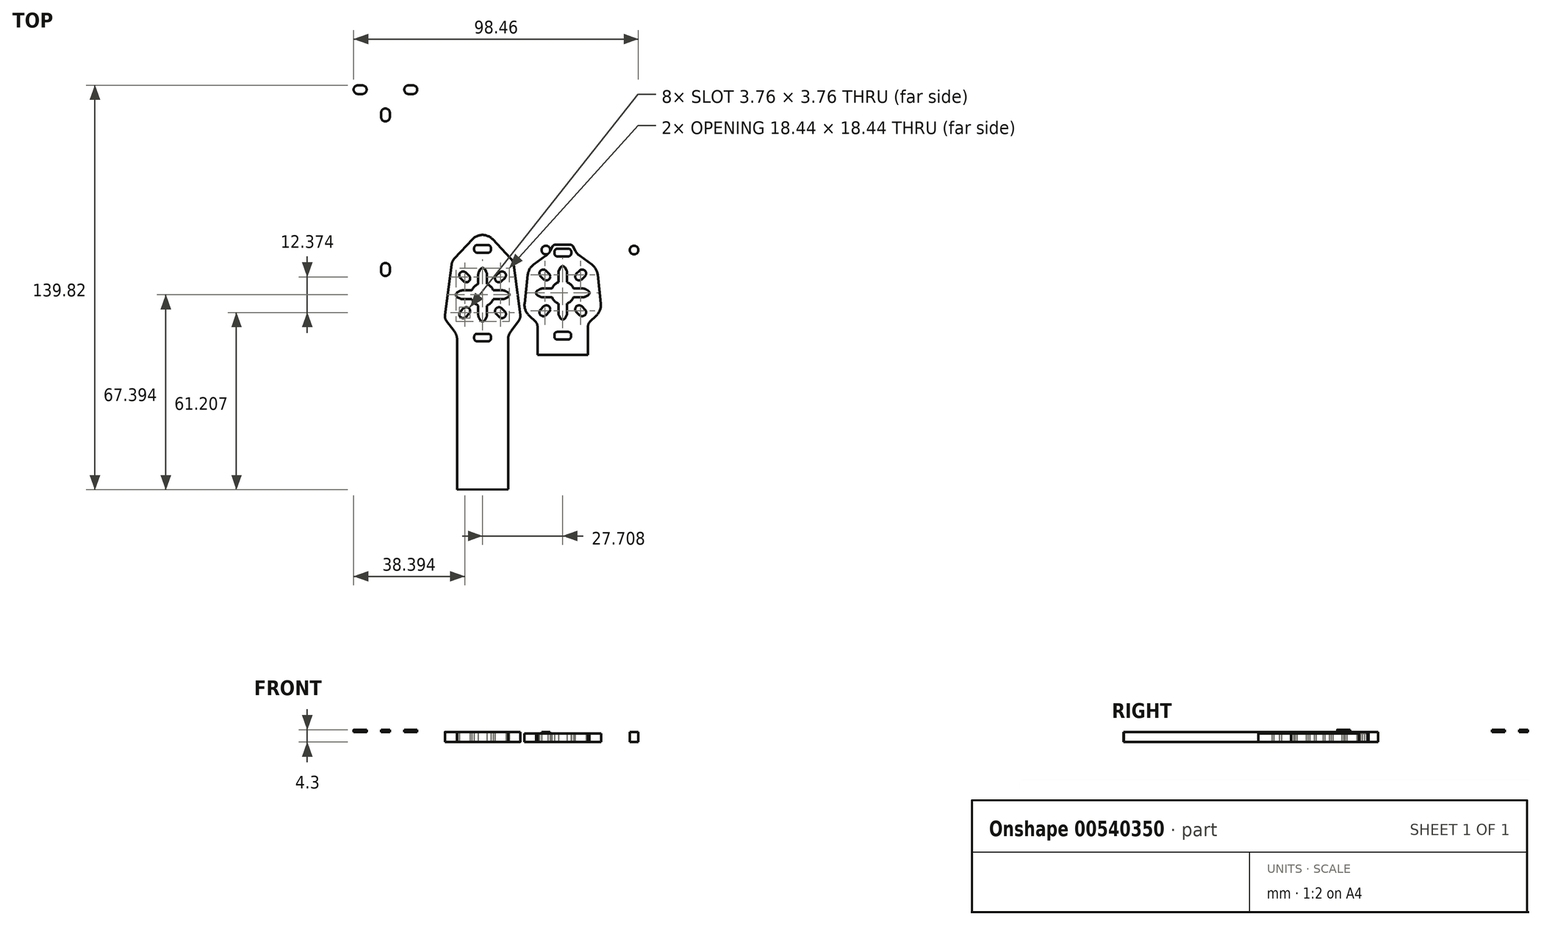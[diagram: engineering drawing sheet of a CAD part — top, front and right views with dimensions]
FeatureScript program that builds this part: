
annotation { "Feature Type Name" : "Feature", "Feature Type Description" : "" }
export const myFeature = defineFeature(function(context is Context, id is Id, definition is map)
    precondition{}
    {
        {
            var Q0;
            Q0=qCreatedBy(makeId("Top.planeOp"),FACE);
            var sketch = newSketch(context, id + "F0", { "sketchPlane" : qUnion([Q0])});
            skCircle(sketch, "E0", {"center": v(0, 0) * mm, "radius": 100 * mm, "construction": true});
            skLineSegment(sketch, "E1.bottom", {"start": v(16, -18) * mm, "end": v(-16, -18) * mm, "construction": true});
            skLineSegment(sketch, "E1.top", {"start": v(16, 18) * mm, "end": v(-16, 18) * mm, "construction": true});
            skLineSegment(sketch, "E1.left", {"start": v(18, -16) * mm, "end": v(18, 16) * mm, "construction": true});
            skLineSegment(sketch, "E1.right", {"start": v(-18, -16) * mm, "end": v(-18, 16) * mm, "construction": true});
            skLineSegment(sketch, "E2", {"start": v(0, 0) * mm, "end": v(-63.94, 63.94) * mm, "construction": true});
            skCircle(sketch, "E3", {"center": v(-15.25, 15.25) * mm, "radius": 1.5 * mm});
            skPoint(sketch, "E4", {"position": v(-37.13, -0.22) * mm});
            skPoint(sketch, "E5.visualSharp", {"position": v(-37.13, -74.76) * mm});
            skArc(sketch, "E5.filletArc", {"start": v(-16, 18) * mm, "mid": v(-17.41, 17.41) * mm, "end": v(-18, 16) * mm, "construction": true});
            skPoint(sketch, "E6.visualSharp", {"position": v(18, 18) * mm});
            skArc(sketch, "E6.filletArc", {"start": v(18, 16) * mm, "mid": v(17.41, 17.41) * mm, "end": v(16, 18) * mm, "construction": true});
            skPoint(sketch, "E7.visualSharp", {"position": v(18, -18) * mm});
            skArc(sketch, "E7.filletArc", {"start": v(16, -18) * mm, "mid": v(17.41, -17.41) * mm, "end": v(18, -16) * mm, "construction": true});
            skPoint(sketch, "E8.visualSharp", {"position": v(-18, -18) * mm});
            skArc(sketch, "E8.filletArc", {"start": v(-18, -16) * mm, "mid": v(-17.41, -17.41) * mm, "end": v(-16, -18) * mm, "construction": true});
            skCircle(sketch, "E9.MirrorC", {"center": v(15.25, 15.25) * mm, "radius": 1.5 * mm});
            skLineSegment(sketch, "E10.bottom", {"start": v(10, -10) * mm, "end": v(-10, -10) * mm, "construction": true});
            skLineSegment(sketch, "E10.top", {"start": v(10, 10) * mm, "end": v(-10, 10) * mm, "construction": true});
            skLineSegment(sketch, "E10.left", {"start": v(10, -10) * mm, "end": v(10, 10) * mm, "construction": true});
            skLineSegment(sketch, "E10.right", {"start": v(-10, -10) * mm, "end": v(-10, 10) * mm, "construction": true});
            skCircle(sketch, "E11", {"center": v(-37.13, -0.22) * mm, "radius": 13.85 * mm, "construction": true});
            skLineSegment(sketch, "E12", {"start": v(-37.13, -0.22) * mm, "end": v(-25.82, -11.53) * mm, "construction": true});
            skArc(sketch, "E13", {"start": v(-30.52, -4.92) * mm, "mid": v(-32.43, -4.92) * mm, "end": v(-32.43, -6.83) * mm});
            skArc(sketch, "E14", {"start": v(-31.37, -7.89) * mm, "mid": v(-29.46, -7.89) * mm, "end": v(-29.46, -5.98) * mm});
            skLineSegment(sketch, "E15", {"start": v(-37.13, -0.22) * mm, "end": v(-58.36, -21.45) * mm, "construction": true});
            skLineSegment(sketch, "E16", {"start": v(-32.43, -6.83) * mm, "end": v(-31.37, -7.89) * mm});
            skLineSegment(sketch, "E17.MirrorCS", {"start": v(-30.52, -4.92) * mm, "end": v(-29.46, -5.98) * mm});
            skLineSegment(sketch, "E18.MirrorCS", {"start": v(-43.74, -4.92) * mm, "end": v(-44.8, -5.98) * mm});
            skArc(sketch, "E19.MirrorCS", {"start": v(-42.9, -7.89) * mm, "mid": v(-44.8, -7.89) * mm, "end": v(-44.8, -5.98) * mm});
            skLineSegment(sketch, "E20.MirrorCS", {"start": v(-41.83, -6.83) * mm, "end": v(-42.9, -7.89) * mm});
            skArc(sketch, "E21.MirrorCS", {"start": v(-43.74, -4.92) * mm, "mid": v(-41.83, -4.92) * mm, "end": v(-41.83, -6.83) * mm});
            skLineSegment(sketch, "E22.MirrorCS", {"start": v(-41.83, 6.4) * mm, "end": v(-42.9, 7.46) * mm});
            skLineSegment(sketch, "E23.MirrorCS", {"start": v(-43.74, 4.49) * mm, "end": v(-44.8, 5.55) * mm});
            skArc(sketch, "E24.MirrorCS", {"start": v(-43.74, 4.49) * mm, "mid": v(-41.83, 4.49) * mm, "end": v(-41.83, 6.4) * mm});
            skArc(sketch, "E25.MirrorCS", {"start": v(-42.9, 7.46) * mm, "mid": v(-44.8, 7.46) * mm, "end": v(-44.8, 5.55) * mm});
            skLineSegment(sketch, "E26.MirrorCS", {"start": v(-32.43, 6.4) * mm, "end": v(-31.37, 7.46) * mm});
            skLineSegment(sketch, "E27.MirrorCS", {"start": v(-30.52, 4.49) * mm, "end": v(-29.46, 5.55) * mm});
            skArc(sketch, "E28.MirrorCS", {"start": v(-31.37, 7.46) * mm, "mid": v(-29.46, 7.46) * mm, "end": v(-29.46, 5.55) * mm});
            skArc(sketch, "E29.MirrorCS", {"start": v(-30.52, 4.49) * mm, "mid": v(-32.43, 4.49) * mm, "end": v(-32.43, 6.4) * mm});
            skLineSegment(sketch, "E30", {"start": v(-26.4, 10.18) * mm, "end": v(-24.12, -7.13) * mm});
            skPoint(sketch, "E31.visualSharp", {"position": v(-26.77, 13.06) * mm});
            skPoint(sketch, "E32.MirrorP", {"position": v(-51, -9.33) * mm});
            skLineSegment(sketch, "E33", {"start": v(-34.22, 15.95) * mm, "end": v(-34.22, 15.34) * mm});
            skLineSegment(sketch, "E34", {"start": v(-40.03, 15.95) * mm, "end": v(-40.03, 15.34) * mm});
            skArc(sketch, "E35", {"start": v(-35.63, -3.92) * mm, "mid": v(-34.3, -3.04) * mm, "end": v(-33.42, -1.72) * mm});
            skLineSegment(sketch, "E36.bottom", {"start": v(-44.11, 1.28) * mm, "end": v(-40.84, 1.28) * mm});
            skLineSegment(sketch, "E36.top", {"start": v(-44.11, -1.72) * mm, "end": v(-40.84, -1.72) * mm});
            skLineSegment(sketch, "E37.left", {"start": v(-38.63, 6.77) * mm, "end": v(-38.63, 3.5) * mm});
            skLineSegment(sketch, "E37.right", {"start": v(-35.63, 6.77) * mm, "end": v(-35.63, 3.5) * mm});
            skLineSegment(sketch, "E38.trimOffspring", {"start": v(-33.42, -1.72) * mm, "end": v(-30.15, -1.72) * mm});
            skLineSegment(sketch, "E39.trimOffspring", {"start": v(-33.42, 1.28) * mm, "end": v(-30.15, 1.28) * mm});
            skLineSegment(sketch, "E40.trimOffspring", {"start": v(-35.63, -3.92) * mm, "end": v(-35.63, -7.2) * mm});
            skLineSegment(sketch, "E41.trimOffspring", {"start": v(-38.63, -3.92) * mm, "end": v(-38.63, -7.2) * mm});
            skArc(sketch, "E42.trimOffspring", {"start": v(-33.42, 1.28) * mm, "mid": v(-34.3, 2.61) * mm, "end": v(-35.63, 3.5) * mm});
            skArc(sketch, "E43.trimOffspring", {"start": v(-38.63, 3.5) * mm, "mid": v(-39.96, 2.61) * mm, "end": v(-40.84, 1.28) * mm});
            skArc(sketch, "E44.trimOffspring", {"start": v(-40.84, -1.72) * mm, "mid": v(-39.96, -3.04) * mm, "end": v(-38.63, -3.92) * mm});
            skArc(sketch, "E45", {"start": v(-27.85, -0.73) * mm, "mid": v(-27.8, -0.7) * mm, "end": v(-27.75, -0.66) * mm});
            skPoint(sketch, "E46.visualSharp", {"position": v(-29.63, -1.72) * mm});
            skArc(sketch, "E46.filletArc", {"start": v(-30.15, -1.72) * mm, "mid": v(-29.65, -1.65) * mm, "end": v(-29.18, -1.46) * mm});
            skPoint(sketch, "E47.visualSharp", {"position": v(-29.63, 1.28) * mm});
            skArc(sketch, "E47.filletArc", {"start": v(-29.18, 1.03) * mm, "mid": v(-29.65, 1.22) * mm, "end": v(-30.15, 1.28) * mm});
            skArc(sketch, "E48.MirrorCS", {"start": v(-45.08, 1.03) * mm, "mid": v(-44.61, 1.22) * mm, "end": v(-44.11, 1.28) * mm});
            skArc(sketch, "E49.MirrorCS", {"start": v(-44.11, -1.72) * mm, "mid": v(-44.61, -1.65) * mm, "end": v(-45.08, -1.46) * mm});
            skArc(sketch, "E50.MirrorCS", {"start": v(-46.4, -0.73) * mm, "mid": v(-46.46, -0.7) * mm, "end": v(-46.5, -0.66) * mm});
            skPoint(sketch, "E51.MirrorP", {"position": v(-44.63, 1.28) * mm});
            skArc(sketch, "E52.MirrorCS", {"start": v(-35.88, -8.17) * mm, "mid": v(-35.7, -7.7) * mm, "end": v(-35.63, -7.2) * mm});
            skArc(sketch, "E53.MirrorCS", {"start": v(-38.63, -7.2) * mm, "mid": v(-38.56, -7.7) * mm, "end": v(-38.38, -8.17) * mm});
            skPoint(sketch, "E54.MirrorP", {"position": v(-35.63, -7.72) * mm});
            skPoint(sketch, "E55.MirrorP", {"position": v(-38.63, -7.72) * mm});
            skArc(sketch, "E56.MirrorCS", {"start": v(-38.63, 6.77) * mm, "mid": v(-38.56, 7.27) * mm, "end": v(-38.38, 7.74) * mm});
            skArc(sketch, "E57.MirrorCS", {"start": v(-35.88, 7.74) * mm, "mid": v(-35.7, 7.27) * mm, "end": v(-35.63, 6.77) * mm});
            skPoint(sketch, "E58.MirrorP", {"position": v(-35.63, 7.28) * mm});
            skPoint(sketch, "E59.MirrorP", {"position": v(-38.63, 7.28) * mm});
            skPoint(sketch, "E60.visualSharp", {"position": v(-34.22, 16.34) * mm});
            skPoint(sketch, "E61.visualSharp", {"position": v(-34.22, 14.34) * mm});
            skArc(sketch, "E61.filletArc", {"start": v(-35.22, 14.34) * mm, "mid": v(-34.52, 14.63) * mm, "end": v(-34.22, 15.34) * mm});
            skPoint(sketch, "E62.visualSharp", {"position": v(-40.03, 14.34) * mm});
            skArc(sketch, "E62.filletArc", {"start": v(-40.03, 15.34) * mm, "mid": v(-39.74, 14.63) * mm, "end": v(-39.03, 14.34) * mm});
            skPoint(sketch, "E63.orphan", {"position": v(-44.63, -1.72) * mm});
            skCircle(sketch, "E64", {"center": v(-37.13, -0.22) * mm, "radius": 8 * mm, "construction": true});
            skLineSegment(sketch, "E65", {"start": v(-27.45, 12.4) * mm, "end": v(-33.62, 18.95) * mm});
            skPoint(sketch, "E66.visualSharp", {"position": v(-26.56, 11.46) * mm});
            skArc(sketch, "E66.filletArc", {"start": v(-26.4, 10.18) * mm, "mid": v(-26.74, 11.37) * mm, "end": v(-27.45, 12.4) * mm});
            skLineSegment(sketch, "E67", {"start": v(-37.13, -0.22) * mm, "end": v(-37.13, -33.93) * mm, "construction": true});
            skLineSegment(sketch, "E68.MirrorCS", {"start": v(-46.8, 12.4) * mm, "end": v(-40.63, 18.95) * mm});
            skLineSegment(sketch, "E69", {"start": v(-24.7, -9.34) * mm, "end": v(-27.3, -12.78) * mm});
            skPoint(sketch, "E70.visualSharp", {"position": v(-23.96, -8.36) * mm});
            skArc(sketch, "E70.filletArc", {"start": v(-24.7, -9.34) * mm, "mid": v(-24.2, -8.3) * mm, "end": v(-24.12, -7.13) * mm});
            skPoint(sketch, "E71.visualSharp", {"position": v(-30.8, -17.37) * mm});
            skArc(sketch, "E72", {"start": v(-33.62, 18.95) * mm, "mid": v(-37.13, 20.46) * mm, "end": v(-40.63, 18.95) * mm});
            skPoint(sketch, "E73.MirrorP", {"position": v(-50.3, -8.36) * mm});
            skPoint(sketch, "E74.MirrorCS.start.orphan", {"position": v(-28.33, -14.12) * mm});
            skPoint(sketch, "E75.MirrorCS.end.orphan", {"position": v(-44.01, -18.06) * mm});
            skPoint(sketch, "E75.MirrorCS.start.orphan", {"position": v(-45.93, -14.12) * mm});
            skPoint(sketch, "E76.MirrorCS.end.orphan", {"position": v(-44.01, -21.74) * mm});
            skPoint(sketch, "E77.end.orphan", {"position": v(-30.25, -21.74) * mm});
            skPoint(sketch, "E77.start.orphan", {"position": v(-30.25, -18.06) * mm});
            skLineSegment(sketch, "E78", {"start": v(-28.33, -15.8) * mm, "end": v(-28.33, -21.65) * mm});
            skArc(sketch, "E79.filletArc", {"start": v(-27.3, -12.78) * mm, "mid": v(-28.06, -14.2) * mm, "end": v(-28.33, -15.8) * mm});
            skPoint(sketch, "E80.visualSharp", {"position": v(-49.56, -9.34) * mm});
            skPoint(sketch, "E81.MirrorCS.start.orphan", {"position": v(-47.87, 10.18) * mm});
            skPoint(sketch, "E82.MirrorCS.end.orphan", {"position": v(-46.8, 12.4) * mm});
            skLineSegment(sketch, "E83.MirrorCS", {"start": v(-47.87, 10.18) * mm, "end": v(-50.14, -7.13) * mm});
            skArc(sketch, "E84.MirrorCS", {"start": v(-47.87, 10.18) * mm, "mid": v(-47.51, 11.37) * mm, "end": v(-46.8, 12.4) * mm});
            skArc(sketch, "E85.MirrorCS", {"start": v(-49.56, -9.34) * mm, "mid": v(-50.07, -8.3) * mm, "end": v(-50.14, -7.13) * mm});
            skLineSegment(sketch, "E86.MirrorCS", {"start": v(-49.56, -9.34) * mm, "end": v(-46.95, -12.78) * mm});
            skArc(sketch, "E87.MirrorCS", {"start": v(-46.95, -12.78) * mm, "mid": v(-46.2, -14.2) * mm, "end": v(-45.93, -15.8) * mm});
            skLineSegment(sketch, "E88.MirrorCS", {"start": v(-45.93, -15.8) * mm, "end": v(-45.93, -21.65) * mm});
            skLineSegment(sketch, "E89", {"start": v(-39.03, 14.34) * mm, "end": v(-35.22, 14.34) * mm});
            skLineSegment(sketch, "E90", {"start": v(-37.13, 15.64) * mm, "end": v(-39.72, 15.64) * mm, "construction": true});
            skArc(sketch, "E91.MirrorCS", {"start": v(-35.22, 16.95) * mm, "mid": v(-34.52, 16.65) * mm, "end": v(-34.22, 15.95) * mm});
            skArc(sketch, "E92.MirrorCS", {"start": v(-40.03, 15.95) * mm, "mid": v(-39.74, 16.65) * mm, "end": v(-39.03, 16.95) * mm});
            skLineSegment(sketch, "E93.MirrorCS", {"start": v(-39.03, 16.95) * mm, "end": v(-35.22, 16.95) * mm});
            skLineSegment(sketch, "E94", {"start": v(-70.71, 70.71) * mm, "end": v(-89.86, 51.56) * mm, "construction": true});
            skLineSegment(sketch, "E95.MirrorCS", {"start": v(-39.03, -13.7) * mm, "end": v(-35.22, -13.7) * mm});
            skArc(sketch, "E96.MirrorCS", {"start": v(-40.03, -14.7) * mm, "mid": v(-39.74, -14) * mm, "end": v(-39.03, -13.7) * mm});
            skArc(sketch, "E97.MirrorCS", {"start": v(-35.22, -13.7) * mm, "mid": v(-34.52, -14) * mm, "end": v(-34.22, -14.7) * mm});
            skLineSegment(sketch, "E98.MirrorCS", {"start": v(-39.03, -16.32) * mm, "end": v(-35.22, -16.32) * mm});
            skArc(sketch, "E99.MirrorCS", {"start": v(-40.03, -15.32) * mm, "mid": v(-39.74, -16.03) * mm, "end": v(-39.03, -16.32) * mm});
            skArc(sketch, "E100.MirrorCS", {"start": v(-35.22, -16.32) * mm, "mid": v(-34.52, -16.03) * mm, "end": v(-34.22, -15.32) * mm});
            skLineSegment(sketch, "E101.MirrorCS", {"start": v(-34.22, -15.32) * mm, "end": v(-34.22, -14.7) * mm});
            skLineSegment(sketch, "E102.MirrorCS", {"start": v(-40.03, -15.32) * mm, "end": v(-40.03, -14.7) * mm});
            skLineSegment(sketch, "E103", {"start": v(-28.33, -21.65) * mm, "end": v(-28.33, -67.5) * mm});
            skLineSegment(sketch, "E104", {"start": v(-45.93, -21.65) * mm, "end": v(-45.93, -67.6) * mm});
            skLineSegment(sketch, "E105", {"start": v(-45.93, -67.6) * mm, "end": v(-28.33, -67.5) * mm});
            skLineSegment(sketch, "E106", {"start": v(-38.38, 7.74) * mm, "end": v(-37.94, 8.52) * mm});
            skLineSegment(sketch, "E107.trimOffspring", {"start": v(-37.13, -9.2) * mm, "end": v(-37.13, 20.66) * mm, "construction": true});
            skPoint(sketch, "E108.trimOffspring.end.orphan", {"position": v(-46.4, 0.3) * mm});
            skLineSegment(sketch, "E109.MirrorCS", {"start": v(-38.38, -8.17) * mm, "end": v(-37.94, -8.96) * mm});
            skPoint(sketch, "E110.orphan", {"position": v(-36.61, -9.5) * mm});
            skPoint(sketch, "E111.MirrorCS.start.orphan", {"position": v(-37.64, -9.5) * mm});
            skLineSegment(sketch, "E112.MirrorCS", {"start": v(-35.88, 7.74) * mm, "end": v(-36.32, 8.52) * mm});
            skArc(sketch, "E113", {"start": v(-36.32, 8.52) * mm, "mid": v(-37.13, 9) * mm, "end": v(-37.94, 8.52) * mm});
            skLineSegment(sketch, "E114.MirrorCS", {"start": v(-35.88, -8.17) * mm, "end": v(-36.32, -8.96) * mm});
            skArc(sketch, "E115.MirrorCS", {"start": v(-36.32, -8.96) * mm, "mid": v(-37.13, -9.43) * mm, "end": v(-37.94, -8.96) * mm});
            skLineSegment(sketch, "E116.MirrorCS", {"start": v(-29.18, 1.03) * mm, "end": v(-28.39, 0.6) * mm});
            skLineSegment(sketch, "E117.MirrorCS", {"start": v(-29.18, -1.46) * mm, "end": v(-28.39, -1.03) * mm});
            skArc(sketch, "E118.MirrorCS", {"start": v(-28.39, 0.6) * mm, "mid": v(-27.91, -0.22) * mm, "end": v(-28.39, -1.03) * mm});
            skLineSegment(sketch, "E119.MirrorCS", {"start": v(-45.08, 1.03) * mm, "end": v(-45.87, 0.6) * mm});
            skLineSegment(sketch, "E120.MirrorCS", {"start": v(-45.08, -1.46) * mm, "end": v(-45.87, -1.03) * mm});
            skArc(sketch, "E121.MirrorCS", {"start": v(-45.87, 0.6) * mm, "mid": v(-46.35, -0.22) * mm, "end": v(-45.87, -1.03) * mm});
            skSolve(sketch);
        }
        {
            var Q0;
            Q0 = qSketchRegion(id + "F0", true);
            extrude(context, id + "F1", {"entities" : qUnion([Q0]), "depth" : 3.5 * mm, "offsetDistance" : 25.4 * mm});
        }
        {
            var Q0;
            Q0=makeQuery(id+"F1.opExtrude","CAP_FACE",FACE,{"disambiguationData":[OSD([sQuery(id+"F0.wireOp",EDGE,"E13"),sQuery(id+"F0.wireOp",EDGE,"E14"),sQuery(id+"F0.wireOp",EDGE,"E16"),sQuery(id+"F0.wireOp",EDGE,"E17.MirrorCS"),sQuery(id+"F0.wireOp",EDGE,"E18.MirrorCS"),sQuery(id+"F0.wireOp",EDGE,"E19.MirrorCS"),sQuery(id+"F0.wireOp",EDGE,"E20.MirrorCS"),sQuery(id+"F0.wireOp",EDGE,"E21.MirrorCS"),sQuery(id+"F0.wireOp",EDGE,"E22.MirrorCS"),sQuery(id+"F0.wireOp",EDGE,"E23.MirrorCS"),sQuery(id+"F0.wireOp",EDGE,"E24.MirrorCS"),sQuery(id+"F0.wireOp",EDGE,"E25.MirrorCS"),sQuery(id+"F0.wireOp",EDGE,"E26.MirrorCS"),sQuery(id+"F0.wireOp",EDGE,"E27.MirrorCS"),sQuery(id+"F0.wireOp",EDGE,"E28.MirrorCS"),sQuery(id+"F0.wireOp",EDGE,"E29.MirrorCS"),sQuery(id+"F0.wireOp",EDGE,"E30"),sQuery(id+"F0.wireOp",EDGE,"E33"),sQuery(id+"F0.wireOp",EDGE,"E34"),sQuery(id+"F0.wireOp",EDGE,"E35"),sQuery(id+"F0.wireOp",EDGE,"E36.bottom"),sQuery(id+"F0.wireOp",EDGE,"E36.top"),sQuery(id+"F0.wireOp",EDGE,"E37.left"),sQuery(id+"F0.wireOp",EDGE,"E37.right"),sQuery(id+"F0.wireOp",EDGE,"E38.trimOffspring"),sQuery(id+"F0.wireOp",EDGE,"E39.trimOffspring"),sQuery(id+"F0.wireOp",EDGE,"E40.trimOffspring"),sQuery(id+"F0.wireOp",EDGE,"E41.trimOffspring"),sQuery(id+"F0.wireOp",EDGE,"E42.trimOffspring"),sQuery(id+"F0.wireOp",EDGE,"E43.trimOffspring"),sQuery(id+"F0.wireOp",EDGE,"E44.trimOffspring"),sQuery(id+"F0.wireOp",EDGE,"E46.filletArc"),sQuery(id+"F0.wireOp",EDGE,"E47.filletArc"),sQuery(id+"F0.wireOp",EDGE,"E48.MirrorCS"),sQuery(id+"F0.wireOp",EDGE,"E49.MirrorCS"),sQuery(id+"F0.wireOp",EDGE,"E52.MirrorCS"),sQuery(id+"F0.wireOp",EDGE,"E53.MirrorCS"),sQuery(id+"F0.wireOp",EDGE,"E56.MirrorCS"),sQuery(id+"F0.wireOp",EDGE,"E57.MirrorCS"),sQuery(id+"F0.wireOp",EDGE,"E61.filletArc"),sQuery(id+"F0.wireOp",EDGE,"E62.filletArc"),sQuery(id+"F0.wireOp",EDGE,"E65"),sQuery(id+"F0.wireOp",EDGE,"E66.filletArc"),sQuery(id+"F0.wireOp",EDGE,"E68.MirrorCS"),sQuery(id+"F0.wireOp",EDGE,"E69"),sQuery(id+"F0.wireOp",EDGE,"E70.filletArc"),sQuery(id+"F0.wireOp",EDGE,"E72"),sQuery(id+"F0.wireOp",EDGE,"E78"),sQuery(id+"F0.wireOp",EDGE,"E79.filletArc"),sQuery(id+"F0.wireOp",EDGE,"E83.MirrorCS"),sQuery(id+"F0.wireOp",EDGE,"E84.MirrorCS"),sQuery(id+"F0.wireOp",EDGE,"E85.MirrorCS"),sQuery(id+"F0.wireOp",EDGE,"E86.MirrorCS"),sQuery(id+"F0.wireOp",EDGE,"E87.MirrorCS"),sQuery(id+"F0.wireOp",EDGE,"E88.MirrorCS"),sQuery(id+"F0.wireOp",EDGE,"E89"),sQuery(id+"F0.wireOp",EDGE,"E91.MirrorCS"),sQuery(id+"F0.wireOp",EDGE,"E92.MirrorCS"),sQuery(id+"F0.wireOp",EDGE,"E93.MirrorCS"),sQuery(id+"F0.wireOp",EDGE,"E95.MirrorCS"),sQuery(id+"F0.wireOp",EDGE,"E96.MirrorCS"),sQuery(id+"F0.wireOp",EDGE,"E97.MirrorCS"),sQuery(id+"F0.wireOp",EDGE,"E98.MirrorCS"),sQuery(id+"F0.wireOp",EDGE,"E99.MirrorCS"),sQuery(id+"F0.wireOp",EDGE,"E100.MirrorCS"),sQuery(id+"F0.wireOp",EDGE,"E101.MirrorCS"),sQuery(id+"F0.wireOp",EDGE,"E102.MirrorCS"),sQuery(id+"F0.wireOp",EDGE,"E103"),sQuery(id+"F0.wireOp",EDGE,"E104"),sQuery(id+"F0.wireOp",EDGE,"E105"),sQuery(id+"F0.wireOp",EDGE,"E106"),sQuery(id+"F0.wireOp",EDGE,"E109.MirrorCS"),sQuery(id+"F0.wireOp",EDGE,"E112.MirrorCS"),sQuery(id+"F0.wireOp",EDGE,"E113"),sQuery(id+"F0.wireOp",EDGE,"E114.MirrorCS"),sQuery(id+"F0.wireOp",EDGE,"E115.MirrorCS"),sQuery(id+"F0.wireOp",EDGE,"E116.MirrorCS"),sQuery(id+"F0.wireOp",EDGE,"E117.MirrorCS"),sQuery(id+"F0.wireOp",EDGE,"E118.MirrorCS"),sQuery(id+"F0.wireOp",EDGE,"E119.MirrorCS"),sQuery(id+"F0.wireOp",EDGE,"E120.MirrorCS"),sQuery(id+"F0.wireOp",EDGE,"E121.MirrorCS")])],"isStart":false});
            var sketch = newSketch(context, id + "F2", { "sketchPlane" : qUnion([Q0])});
            skArc(sketch, "E122", {"start": v(-40.92, 1.05) * mm, "mid": v(-41.13, -0.22) * mm, "end": v(-40.92, -1.48) * mm});
            skArc(sketch, "E123.trimOffspring", {"start": v(-35.79, 3.55) * mm, "mid": v(-37.13, 3.78) * mm, "end": v(-38.47, 3.55) * mm});
            skArc(sketch, "E124.trimOffspring", {"start": v(-33.34, -1.48) * mm, "mid": v(-33.13, -0.22) * mm, "end": v(-33.34, 1.05) * mm});
            skArc(sketch, "E125.trimOffspring", {"start": v(-38.47, -3.98) * mm, "mid": v(-37.13, -4.22) * mm, "end": v(-35.79, -3.98) * mm});
            skArc(sketch, "E126", {"start": v(-69.21, 9.28) * mm, "mid": v(-70.71, 10.78) * mm, "end": v(-72.21, 9.28) * mm});
            skPoint(sketch, "E127.center.orphan", {"position": v(-70.71, 7.78) * mm});
            skArc(sketch, "E128", {"start": v(-72.21, 7.78) * mm, "mid": v(-70.71, 6.28) * mm, "end": v(-69.21, 7.78) * mm});
            skLineSegment(sketch, "E129", {"start": v(-69.21, 9.28) * mm, "end": v(-69.21, 7.78) * mm});
            skLineSegment(sketch, "E130", {"start": v(-72.21, 9.28) * mm, "end": v(-72.21, 7.78) * mm});
            skArc(sketch, "E131", {"start": v(-32.49, 10.63) * mm, "mid": v(-36.77, 11.58) * mm, "end": v(-41.1, 10.9) * mm});
            skLineSegment(sketch, "E132", {"start": v(-38.47, 3.55) * mm, "end": v(-41.3, 6.38) * mm});
            skLineSegment(sketch, "E133", {"start": v(-40.92, 1.05) * mm, "end": v(-43.75, 3.88) * mm});
            skArc(sketch, "E134", {"start": v(-41.3, 6.38) * mm, "mid": v(-43.79, 6.37) * mm, "end": v(-43.75, 3.88) * mm});
            skArc(sketch, "E135", {"start": v(-42.27, 8.55) * mm, "mid": v(-43.34, 7.83) * mm, "end": v(-44.32, 6.97) * mm});
            skLineSegment(sketch, "E136", {"start": v(-41.77, 9.95) * mm, "end": v(-41.77, 9.42) * mm});
            skPoint(sketch, "E137.visualSharp", {"position": v(-41.77, 8.83) * mm});
            skArc(sketch, "E137.filletArc", {"start": v(-42.27, 8.55) * mm, "mid": v(-41.9, 8.92) * mm, "end": v(-41.77, 9.42) * mm});
            skPoint(sketch, "E138.visualSharp", {"position": v(-41.77, 10.63) * mm});
            skArc(sketch, "E138.filletArc", {"start": v(-41.1, 10.9) * mm, "mid": v(-41.59, 10.53) * mm, "end": v(-41.77, 9.95) * mm});
            skLineSegment(sketch, "E139.MirrorCS", {"start": v(-66.07, 80.88) * mm, "end": v(-66.07, 80.34) * mm});
            skArc(sketch, "E140.MirrorCS", {"start": v(-65.57, 79.48) * mm, "mid": v(-65.94, 79.85) * mm, "end": v(-66.07, 80.34) * mm});
            skArc(sketch, "E141.MirrorCS", {"start": v(-65.57, 79.48) * mm, "mid": v(-64.5, 78.75) * mm, "end": v(-63.52, 77.9) * mm});
            skPoint(sketch, "E142.MirrorP", {"position": v(-66.07, 79.75) * mm});
            skPoint(sketch, "E143.MirrorP", {"position": v(-66.07, 81.56) * mm});
            skPoint(sketch, "E144.MirrorP", {"position": v(-32.49, 10.63) * mm});
            skArc(sketch, "E145.MirrorCS", {"start": v(-66.73, 81.82) * mm, "mid": v(-66.25, 81.45) * mm, "end": v(-66.07, 80.88) * mm});
            skLineSegment(sketch, "E146.MirrorCS", {"start": v(-69.37, 74.48) * mm, "end": v(-66.54, 77.3) * mm});
            skArc(sketch, "E147.MirrorCS", {"start": v(-66.54, 77.3) * mm, "mid": v(-64.05, 77.3) * mm, "end": v(-64.09, 74.8) * mm});
            skLineSegment(sketch, "E148.MirrorCS", {"start": v(-66.92, 71.98) * mm, "end": v(-64.09, 74.8) * mm});
            skLineSegment(sketch, "E149.MirrorCS", {"start": v(-66.07, 60.54) * mm, "end": v(-66.07, 61.08) * mm});
            skLineSegment(sketch, "E150.MirrorCS", {"start": v(-75.35, 60.54) * mm, "end": v(-75.35, 61.08) * mm});
            skArc(sketch, "E151.MirrorCS", {"start": v(-75.85, 61.94) * mm, "mid": v(-75.49, 61.57) * mm, "end": v(-75.35, 61.08) * mm});
            skPoint(sketch, "E152.MirrorP", {"position": v(-66.07, 59.86) * mm});
            skArc(sketch, "E153.MirrorCS", {"start": v(-74.7, 59.6) * mm, "mid": v(-75.17, 59.97) * mm, "end": v(-75.35, 60.54) * mm});
            skArc(sketch, "E154.MirrorCS", {"start": v(-66.73, 59.6) * mm, "mid": v(-66.25, 59.97) * mm, "end": v(-66.07, 60.54) * mm});
            skArc(sketch, "E155.MirrorCS", {"start": v(-65.57, 61.94) * mm, "mid": v(-65.94, 61.57) * mm, "end": v(-66.07, 61.08) * mm});
            skArc(sketch, "E156.MirrorCS", {"start": v(-74.88, 64.11) * mm, "mid": v(-77.37, 64.13) * mm, "end": v(-77.33, 66.61) * mm});
            skArc(sketch, "E157.MirrorCS", {"start": v(-75.85, 61.94) * mm, "mid": v(-76.92, 62.67) * mm, "end": v(-77.9, 63.52) * mm});
            skPoint(sketch, "E158.MirrorP", {"position": v(-75.35, 61.67) * mm});
            skLineSegment(sketch, "E159.MirrorCS", {"start": v(-69.21, 61.21) * mm, "end": v(-69.21, 62.71) * mm});
            skArc(sketch, "E160.MirrorCS", {"start": v(-69.37, 66.94) * mm, "mid": v(-70.71, 66.71) * mm, "end": v(-72.05, 66.94) * mm});
            skLineSegment(sketch, "E161.MirrorCS", {"start": v(-72.21, 61.21) * mm, "end": v(-72.21, 62.71) * mm});
            skArc(sketch, "E162.MirrorCS", {"start": v(-72.21, 62.71) * mm, "mid": v(-70.71, 64.21) * mm, "end": v(-69.21, 62.71) * mm});
            skPoint(sketch, "E163.MirrorP", {"position": v(-75.35, 59.86) * mm});
            skArc(sketch, "E164.MirrorCS", {"start": v(-65.57, 61.94) * mm, "mid": v(-64.5, 62.67) * mm, "end": v(-63.52, 63.52) * mm});
            skLineSegment(sketch, "E165.MirrorCS", {"start": v(-72.05, 66.94) * mm, "end": v(-74.88, 64.11) * mm});
            skPoint(sketch, "E166.MirrorP", {"position": v(-66.07, 61.67) * mm});
            skArc(sketch, "E167.MirrorCS", {"start": v(-69.21, 61.21) * mm, "mid": v(-70.71, 59.71) * mm, "end": v(-72.21, 61.21) * mm});
            skArc(sketch, "E168.MirrorCS", {"start": v(-66.54, 64.11) * mm, "mid": v(-64.05, 64.13) * mm, "end": v(-64.09, 66.61) * mm});
            skLineSegment(sketch, "E169.MirrorCS", {"start": v(-69.37, 66.94) * mm, "end": v(-66.54, 64.11) * mm});
            skLineSegment(sketch, "E170.MirrorCS", {"start": v(-74.5, 69.44) * mm, "end": v(-77.33, 66.61) * mm});
            skLineSegment(sketch, "E171.MirrorCS", {"start": v(-66.92, 69.44) * mm, "end": v(-64.09, 66.61) * mm});
            skArc(sketch, "E172.MirrorCS", {"start": v(-66.07, 59.86) * mm, "mid": v(-70.35, 58.92) * mm, "end": v(-74.7, 59.6) * mm});
            skLineSegment(sketch, "E173.MirrorCS", {"start": v(-60.54, 75.35) * mm, "end": v(-61.08, 75.35) * mm});
            skLineSegment(sketch, "E174.MirrorCS", {"start": v(-60.54, 66.07) * mm, "end": v(-61.08, 66.07) * mm});
            skArc(sketch, "E175.MirrorCS", {"start": v(-61.94, 75.85) * mm, "mid": v(-61.57, 75.49) * mm, "end": v(-61.08, 75.35) * mm});
            skArc(sketch, "E176.MirrorCS", {"start": v(-59.6, 66.73) * mm, "mid": v(-59.97, 66.25) * mm, "end": v(-60.54, 66.07) * mm});
            skArc(sketch, "E177.MirrorCS", {"start": v(-59.6, 74.7) * mm, "mid": v(-59.97, 75.17) * mm, "end": v(-60.54, 75.35) * mm});
            skPoint(sketch, "E178.MirrorP", {"position": v(-59.86, 75.35) * mm});
            skArc(sketch, "E179.MirrorCS", {"start": v(-61.94, 65.57) * mm, "mid": v(-61.57, 65.94) * mm, "end": v(-61.08, 66.07) * mm});
            skArc(sketch, "E180.MirrorCS", {"start": v(-61.94, 65.57) * mm, "mid": v(-62.67, 64.5) * mm, "end": v(-63.52, 63.52) * mm});
            skLineSegment(sketch, "E181.MirrorCS", {"start": v(-61.21, 72.21) * mm, "end": v(-62.71, 72.21) * mm});
            skPoint(sketch, "E182.MirrorP", {"position": v(-61.67, 66.07) * mm});
            skArc(sketch, "E183.MirrorCS", {"start": v(-59.6, 74.7) * mm, "mid": v(-58.91, 70.71) * mm, "end": v(-59.6, 66.73) * mm});
            skPoint(sketch, "E184.MirrorP", {"position": v(-59.86, 66.07) * mm});
            skPoint(sketch, "E185.MirrorP", {"position": v(-62.71, 70.71) * mm});
            skArc(sketch, "E186.MirrorCS", {"start": v(-61.94, 75.85) * mm, "mid": v(-62.67, 76.92) * mm, "end": v(-63.52, 77.9) * mm});
            skPoint(sketch, "E187.MirrorP", {"position": v(-61.67, 75.35) * mm});
            skLineSegment(sketch, "E188.MirrorCS", {"start": v(-61.21, 69.21) * mm, "end": v(-62.71, 69.21) * mm});
            skArc(sketch, "E189.MirrorCS", {"start": v(-61.21, 72.21) * mm, "mid": v(-59.71, 70.71) * mm, "end": v(-61.21, 69.21) * mm});
            skArc(sketch, "E190.MirrorCS", {"start": v(-62.71, 69.21) * mm, "mid": v(-64.21, 70.71) * mm, "end": v(-62.71, 72.21) * mm});
            skLineSegment(sketch, "E191.MirrorCS", {"start": v(-80.21, 72.21) * mm, "end": v(-78.71, 72.21) * mm});
            skLineSegment(sketch, "E192.MirrorCS", {"start": v(-80.21, 69.21) * mm, "end": v(-78.71, 69.21) * mm});
            skArc(sketch, "E193.MirrorCS", {"start": v(-78.71, 69.21) * mm, "mid": v(-77.21, 70.71) * mm, "end": v(-78.71, 72.21) * mm});
            skArc(sketch, "E194.MirrorCS", {"start": v(-80.21, 72.21) * mm, "mid": v(-81.71, 70.71) * mm, "end": v(-80.21, 69.21) * mm});
            skLineSegment(sketch, "E195.MirrorCS", {"start": v(-75.35, 80.88) * mm, "end": v(-75.35, 80.34) * mm});
            skArc(sketch, "E196.MirrorCS", {"start": v(-75.85, 79.48) * mm, "mid": v(-75.49, 79.85) * mm, "end": v(-75.35, 80.34) * mm});
            skArc(sketch, "E197.MirrorCS", {"start": v(-74.7, 81.82) * mm, "mid": v(-75.17, 81.45) * mm, "end": v(-75.35, 80.88) * mm});
            skPoint(sketch, "E198.MirrorP", {"position": v(-75.35, 81.56) * mm});
            skArc(sketch, "E199.MirrorCS", {"start": v(-75.85, 79.48) * mm, "mid": v(-76.92, 78.75) * mm, "end": v(-77.9, 77.9) * mm});
            skPoint(sketch, "E200.MirrorP", {"position": v(-75.35, 79.75) * mm});
            skArc(sketch, "E201.MirrorCS", {"start": v(-45.9, 4.92) * mm, "mid": v(-45.17, 6) * mm, "end": v(-44.32, 6.97) * mm});
            skLineSegment(sketch, "E202.MirrorCS", {"start": v(-80.88, 66.07) * mm, "end": v(-80.34, 66.07) * mm});
            skArc(sketch, "E203.MirrorCS", {"start": v(-79.48, 65.57) * mm, "mid": v(-79.85, 65.94) * mm, "end": v(-80.34, 66.07) * mm});
            skPoint(sketch, "E204.MirrorP", {"position": v(-79.75, 66.07) * mm});
            skPoint(sketch, "E205.MirrorP", {"position": v(-81.56, 66.07) * mm});
            skArc(sketch, "E206.MirrorCS", {"start": v(-79.48, 65.57) * mm, "mid": v(-78.75, 64.5) * mm, "end": v(-77.9, 63.52) * mm});
            skLineSegment(sketch, "E207.MirrorCS", {"start": v(-80.88, 75.35) * mm, "end": v(-80.34, 75.35) * mm});
            skArc(sketch, "E208.MirrorCS", {"start": v(-81.82, 74.7) * mm, "mid": v(-81.45, 75.17) * mm, "end": v(-80.88, 75.35) * mm});
            skArc(sketch, "E209.MirrorCS", {"start": v(-79.48, 75.85) * mm, "mid": v(-79.85, 75.49) * mm, "end": v(-80.34, 75.35) * mm});
            skPoint(sketch, "E210.MirrorP", {"position": v(-81.56, 75.35) * mm});
            skPoint(sketch, "E211.MirrorP", {"position": v(-79.75, 75.35) * mm});
            skArc(sketch, "E212.MirrorCS", {"start": v(-81.82, 74.7) * mm, "mid": v(-82.51, 70.71) * mm, "end": v(-81.82, 66.73) * mm});
            skArc(sketch, "E213.MirrorCS", {"start": v(-81.82, 66.73) * mm, "mid": v(-81.45, 66.25) * mm, "end": v(-80.88, 66.07) * mm});
            skSolve(sketch);
        }
        {
            var Q0;
            Q0 = qSketchRegion(id + "F2", true);
            extrude(context, id + "F3", {"entities" : qUnion([Q0]), "depth" : 0.8 * mm, "offsetDistance" : 25 * mm});
        }
        {
            var Q0;
            Q0=qCreatedBy(makeId("Top.planeOp"),FACE);
            var sketch = newSketch(context, id + "F4", { "sketchPlane" : qUnion([Q0])});
            skPoint(sketch, "E214.visualSharp", {"position": v(8.94, -5.4) * mm});
            skCircle(sketch, "E215", {"center": v(-9.42, 0.43) * mm, "radius": 13.85 * mm, "construction": true});
            skLineSegment(sketch, "E216", {"start": v(-9.42, 0.43) * mm, "end": v(1.9, -10.88) * mm, "construction": true});
            skArc(sketch, "E217", {"start": v(-2.8, -4.27) * mm, "mid": v(-4.72, -4.27) * mm, "end": v(-4.72, -6.18) * mm});
            skArc(sketch, "E218", {"start": v(-3.66, -7.24) * mm, "mid": v(-1.75, -7.24) * mm, "end": v(-1.75, -5.33) * mm});
            skLineSegment(sketch, "E219", {"start": v(-4.72, -6.18) * mm, "end": v(-3.66, -7.24) * mm});
            skLineSegment(sketch, "E220.MirrorCS", {"start": v(-2.8, -4.27) * mm, "end": v(-1.75, -5.33) * mm});
            skLineSegment(sketch, "E221.MirrorCS", {"start": v(-16.03, -4.27) * mm, "end": v(-17.1, -5.33) * mm});
            skArc(sketch, "E222.MirrorCS", {"start": v(-15.18, -7.24) * mm, "mid": v(-17.1, -7.24) * mm, "end": v(-17.1, -5.33) * mm});
            skLineSegment(sketch, "E223.MirrorCS", {"start": v(-14.12, -6.18) * mm, "end": v(-15.18, -7.24) * mm});
            skArc(sketch, "E224.MirrorCS", {"start": v(-16.03, -4.27) * mm, "mid": v(-14.12, -4.27) * mm, "end": v(-14.12, -6.18) * mm});
            skLineSegment(sketch, "E225.MirrorCS", {"start": v(-14.12, 7.05) * mm, "end": v(-15.18, 8.1) * mm});
            skLineSegment(sketch, "E226.MirrorCS", {"start": v(-16.03, 5.14) * mm, "end": v(-17.1, 6.2) * mm});
            skArc(sketch, "E227.MirrorCS", {"start": v(-16.03, 5.14) * mm, "mid": v(-14.12, 5.14) * mm, "end": v(-14.12, 7.05) * mm});
            skArc(sketch, "E228.MirrorCS", {"start": v(-15.18, 8.1) * mm, "mid": v(-17.1, 8.1) * mm, "end": v(-17.1, 6.2) * mm});
            skLineSegment(sketch, "E229.MirrorCS", {"start": v(-4.72, 7.05) * mm, "end": v(-3.66, 8.1) * mm});
            skLineSegment(sketch, "E230.MirrorCS", {"start": v(-2.8, 5.14) * mm, "end": v(-1.75, 6.2) * mm});
            skArc(sketch, "E231.MirrorCS", {"start": v(-3.66, 8.1) * mm, "mid": v(-1.75, 8.1) * mm, "end": v(-1.75, 6.2) * mm});
            skArc(sketch, "E232.MirrorCS", {"start": v(-2.8, 5.14) * mm, "mid": v(-4.72, 5.14) * mm, "end": v(-4.72, 7.05) * mm});
            skLineSegment(sketch, "E233", {"start": v(-6.48, 14.68) * mm, "end": v(-6.48, 14.07) * mm});
            skLineSegment(sketch, "E234", {"start": v(-12.3, 14.68) * mm, "end": v(-12.3, 14.07) * mm});
            skArc(sketch, "E235", {"start": v(-7.92, -3.27) * mm, "mid": v(-6.6, -2.4) * mm, "end": v(-5.71, -1.07) * mm});
            skLineSegment(sketch, "E236.bottom", {"start": v(-16.4, 1.93) * mm, "end": v(-13.13, 1.93) * mm});
            skLineSegment(sketch, "E236.top", {"start": v(-16.4, -1.07) * mm, "end": v(-13.13, -1.07) * mm});
            skLineSegment(sketch, "E237.left", {"start": v(-10.92, 7.42) * mm, "end": v(-10.92, 4.14) * mm});
            skLineSegment(sketch, "E237.right", {"start": v(-7.92, 7.42) * mm, "end": v(-7.92, 4.14) * mm});
            skLineSegment(sketch, "E238.trimOffspring", {"start": v(-5.71, -1.07) * mm, "end": v(-2.44, -1.07) * mm});
            skLineSegment(sketch, "E239.trimOffspring", {"start": v(-5.71, 1.93) * mm, "end": v(-2.44, 1.93) * mm});
            skLineSegment(sketch, "E240.trimOffspring", {"start": v(-7.92, -3.27) * mm, "end": v(-7.92, -6.55) * mm});
            skLineSegment(sketch, "E241.trimOffspring", {"start": v(-10.92, -3.27) * mm, "end": v(-10.92, -6.55) * mm});
            skArc(sketch, "E242.trimOffspring", {"start": v(-5.71, 1.93) * mm, "mid": v(-6.6, 3.26) * mm, "end": v(-7.92, 4.14) * mm});
            skArc(sketch, "E243.trimOffspring", {"start": v(-10.92, 4.14) * mm, "mid": v(-12.25, 3.26) * mm, "end": v(-13.13, 1.93) * mm});
            skArc(sketch, "E244.trimOffspring", {"start": v(-13.13, -1.07) * mm, "mid": v(-12.25, -2.4) * mm, "end": v(-10.92, -3.27) * mm});
            skArc(sketch, "E245", {"start": v(-0.14, -0.08) * mm, "mid": v(-0.1, -0.05) * mm, "end": v(-0.04, 0) * mm});
            skArc(sketch, "E246.filletArc", {"start": v(-2.44, -1.07) * mm, "mid": v(-1.94, -1) * mm, "end": v(-1.47, -0.81) * mm});
            skArc(sketch, "E247.filletArc", {"start": v(-1.47, 1.68) * mm, "mid": v(-1.94, 1.87) * mm, "end": v(-2.44, 1.93) * mm});
            skArc(sketch, "E248.MirrorCS", {"start": v(-17.37, 1.68) * mm, "mid": v(-16.9, 1.87) * mm, "end": v(-16.4, 1.93) * mm});
            skArc(sketch, "E249.MirrorCS", {"start": v(-16.4, -1.07) * mm, "mid": v(-16.9, -1) * mm, "end": v(-17.37, -0.81) * mm});
            skArc(sketch, "E250.MirrorCS", {"start": v(-18.7, -0.08) * mm, "mid": v(-18.75, -0.05) * mm, "end": v(-18.8, 0) * mm});
            skArc(sketch, "E251.MirrorCS", {"start": v(-8.17, -7.52) * mm, "mid": v(-7.98, -7.05) * mm, "end": v(-7.92, -6.55) * mm});
            skArc(sketch, "E252.MirrorCS", {"start": v(-10.92, -6.55) * mm, "mid": v(-10.86, -7.05) * mm, "end": v(-10.67, -7.52) * mm});
            skArc(sketch, "E253.MirrorCS", {"start": v(-10.92, 7.42) * mm, "mid": v(-10.86, 7.92) * mm, "end": v(-10.67, 8.39) * mm});
            skArc(sketch, "E254.MirrorCS", {"start": v(-8.17, 8.39) * mm, "mid": v(-7.98, 7.92) * mm, "end": v(-7.92, 7.42) * mm});
            skArc(sketch, "E255.filletArc", {"start": v(-7.48, 13.07) * mm, "mid": v(-6.78, 13.36) * mm, "end": v(-6.48, 14.07) * mm});
            skArc(sketch, "E256.filletArc", {"start": v(-12.3, 14.07) * mm, "mid": v(-12, 13.36) * mm, "end": v(-11.3, 13.07) * mm});
            skCircle(sketch, "E257", {"center": v(-9.42, 0.43) * mm, "radius": 8 * mm, "construction": true});
            skLineSegment(sketch, "E258.MirrorCS", {"start": v(-18.17, -11.07) * mm, "end": v(-18.17, -21) * mm});
            skLineSegment(sketch, "E259", {"start": v(-11.3, 13.07) * mm, "end": v(-7.48, 13.07) * mm});
            skArc(sketch, "E260.MirrorCS", {"start": v(-7.48, 15.68) * mm, "mid": v(-6.78, 15.38) * mm, "end": v(-6.48, 14.68) * mm});
            skArc(sketch, "E261.MirrorCS", {"start": v(-12.3, 14.68) * mm, "mid": v(-12, 15.38) * mm, "end": v(-11.3, 15.68) * mm});
            skLineSegment(sketch, "E262.MirrorCS", {"start": v(-11.3, 15.68) * mm, "end": v(-7.48, 15.68) * mm});
            skLineSegment(sketch, "E263.MirrorCS", {"start": v(-11.33, -13.06) * mm, "end": v(-7.52, -13.06) * mm});
            skArc(sketch, "E264.MirrorCS", {"start": v(-12.33, -14.06) * mm, "mid": v(-12.03, -13.35) * mm, "end": v(-11.33, -13.06) * mm});
            skArc(sketch, "E265.MirrorCS", {"start": v(-7.52, -13.06) * mm, "mid": v(-6.8, -13.35) * mm, "end": v(-6.52, -14.06) * mm});
            skLineSegment(sketch, "E266.MirrorCS", {"start": v(-11.33, -15.67) * mm, "end": v(-7.52, -15.67) * mm});
            skArc(sketch, "E267.MirrorCS", {"start": v(-12.33, -14.67) * mm, "mid": v(-12.03, -15.38) * mm, "end": v(-11.33, -15.67) * mm});
            skArc(sketch, "E268.MirrorCS", {"start": v(-7.52, -15.67) * mm, "mid": v(-6.8, -15.38) * mm, "end": v(-6.52, -14.67) * mm});
            skLineSegment(sketch, "E269.MirrorCS", {"start": v(-6.52, -14.67) * mm, "end": v(-6.52, -14.06) * mm});
            skLineSegment(sketch, "E270.MirrorCS", {"start": v(-12.33, -14.67) * mm, "end": v(-12.33, -14.06) * mm});
            skLineSegment(sketch, "E271", {"start": v(-10.67, 8.39) * mm, "end": v(-10.23, 9.17) * mm});
            skLineSegment(sketch, "E272.trimOffspring", {"start": v(-9.42, -8.56) * mm, "end": v(-9.42, 21.3) * mm, "construction": true});
            skLineSegment(sketch, "E273.MirrorCS", {"start": v(-10.67, -7.52) * mm, "end": v(-10.23, -8.3) * mm});
            skLineSegment(sketch, "E274.MirrorCS", {"start": v(-8.17, 8.39) * mm, "end": v(-8.6, 9.17) * mm});
            skArc(sketch, "E275", {"start": v(-8.6, 9.17) * mm, "mid": v(-9.42, 9.65) * mm, "end": v(-10.23, 9.17) * mm});
            skLineSegment(sketch, "E276.MirrorCS", {"start": v(-8.17, -7.52) * mm, "end": v(-8.6, -8.3) * mm});
            skArc(sketch, "E277.MirrorCS", {"start": v(-8.6, -8.3) * mm, "mid": v(-9.42, -8.78) * mm, "end": v(-10.23, -8.3) * mm});
            skLineSegment(sketch, "E278.MirrorCS", {"start": v(-1.47, 1.68) * mm, "end": v(-0.68, 1.25) * mm});
            skLineSegment(sketch, "E279.MirrorCS", {"start": v(-1.47, -0.81) * mm, "end": v(-0.68, -0.38) * mm});
            skArc(sketch, "E280.MirrorCS", {"start": v(-0.68, 1.25) * mm, "mid": v(-0.2, 0.43) * mm, "end": v(-0.68, -0.38) * mm});
            skLineSegment(sketch, "E281.MirrorCS", {"start": v(-17.37, 1.68) * mm, "end": v(-18.16, 1.25) * mm});
            skLineSegment(sketch, "E282.MirrorCS", {"start": v(-17.37, -0.81) * mm, "end": v(-18.16, -0.38) * mm});
            skArc(sketch, "E283.MirrorCS", {"start": v(-18.16, 1.25) * mm, "mid": v(-18.64, 0.43) * mm, "end": v(-18.16, -0.38) * mm});
            skPoint(sketch, "E284.visualSharp", {"position": v(-21.26, 8.44) * mm});
            skPoint(sketch, "E285.endSnap0", {"position": v(-14.12, -4.27) * mm});
            skLineSegment(sketch, "E286", {"start": v(-21.5, 6.74) * mm, "end": v(-22.6, -3.18) * mm});
            skPoint(sketch, "E287.visualSharp", {"position": v(-18.17, -10.3) * mm});
            skArc(sketch, "E287.filletArc", {"start": v(-18.17, -11.07) * mm, "mid": v(-18.3, -10.36) * mm, "end": v(-18.67, -9.74) * mm});
            skArc(sketch, "E288.MirrorCS", {"start": v(-0.68, -11.07) * mm, "mid": v(-0.54, -10.36) * mm, "end": v(-0.17, -9.74) * mm});
            skLineSegment(sketch, "E289.MirrorCS", {"start": v(-0.68, -11.07) * mm, "end": v(-0.68, -21) * mm});
            skLineSegment(sketch, "E290", {"start": v(-18.17, -21) * mm, "end": v(-0.68, -21) * mm});
            skLineSegment(sketch, "E291", {"start": v(-13.8, 14.94) * mm, "end": v(-12.9, 16.56) * mm});
            skPoint(sketch, "E292.visualSharp", {"position": v(-14.34, 13.93) * mm});
            skArc(sketch, "E292.filletArc", {"start": v(-15.28, 13.27) * mm, "mid": v(-14.44, 14.02) * mm, "end": v(-13.8, 14.94) * mm});
            skPoint(sketch, "E293.visualSharp", {"position": v(-12.5, 17.32) * mm});
            skArc(sketch, "E294.MirrorCS", {"start": v(-3.56, 13.27) * mm, "mid": v(-4.4, 14.02) * mm, "end": v(-5.05, 14.94) * mm});
            skLineSegment(sketch, "E295.MirrorCS", {"start": v(-5.05, 14.94) * mm, "end": v(-5.94, 16.56) * mm});
            skLineSegment(sketch, "E296", {"start": v(-15.28, 13.27) * mm, "end": v(-19.47, 10.23) * mm});
            skLineSegment(sketch, "E297", {"start": v(-18.67, -9.74) * mm, "end": v(-21.15, -7.3) * mm});
            skPoint(sketch, "E298.visualSharp", {"position": v(-22.87, -5.6) * mm});
            skArc(sketch, "E298.filletArc", {"start": v(-22.6, -3.18) * mm, "mid": v(-22.35, -5.4) * mm, "end": v(-21.15, -7.3) * mm});
            skPoint(sketch, "E299.visualSharp", {"position": v(-21.26, 8.93) * mm});
            skArc(sketch, "E299.filletArc", {"start": v(-19.47, 10.23) * mm, "mid": v(-20.85, 8.7) * mm, "end": v(-21.5, 6.74) * mm});
            skLineSegment(sketch, "E300.MirrorCS", {"start": v(-3.56, 13.27) * mm, "end": v(0.62, 10.23) * mm});
            skArc(sketch, "E301.MirrorCS", {"start": v(0.62, 10.23) * mm, "mid": v(2.01, 8.7) * mm, "end": v(2.66, 6.74) * mm});
            skLineSegment(sketch, "E302.MirrorCS", {"start": v(2.66, 6.74) * mm, "end": v(3.76, -3.18) * mm});
            skArc(sketch, "E303.MirrorCS", {"start": v(3.76, -3.18) * mm, "mid": v(3.5, -5.4) * mm, "end": v(2.3, -7.3) * mm});
            skLineSegment(sketch, "E304.MirrorCS", {"start": v(-0.17, -9.74) * mm, "end": v(2.3, -7.3) * mm});
            skLineSegment(sketch, "E305", {"start": v(-12.03, 17.08) * mm, "end": v(-6.81, 17.08) * mm});
            skPoint(sketch, "E306.visualSharp", {"position": v(-12.62, 17.08) * mm});
            skArc(sketch, "E306.filletArc", {"start": v(-12.03, 17.08) * mm, "mid": v(-12.54, 16.94) * mm, "end": v(-12.9, 16.56) * mm});
            skPoint(sketch, "E307.visualSharp", {"position": v(-6.22, 17.08) * mm});
            skArc(sketch, "E307.filletArc", {"start": v(-5.94, 16.56) * mm, "mid": v(-6.3, 16.94) * mm, "end": v(-6.81, 17.08) * mm});
            skSolve(sketch);
        }
        {
            var Q0;
            Q0 = qSketchRegion(id + "F4", true);
            extrude(context, id + "F5", {"entities" : qUnion([Q0]), "operationType" : NewBodyOperationType.ADD, "depth" : 3 * mm, "offsetDistance" : 25 * mm});
        }
    });
